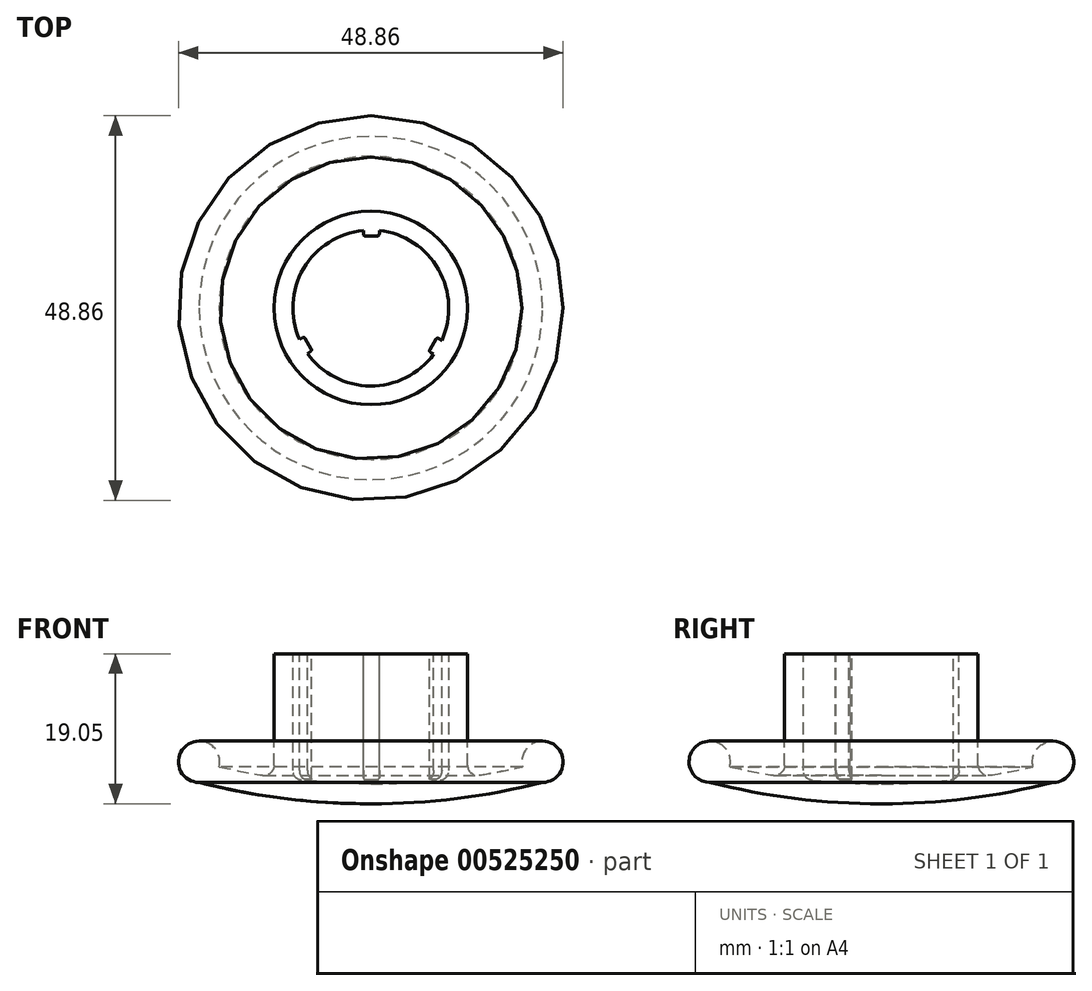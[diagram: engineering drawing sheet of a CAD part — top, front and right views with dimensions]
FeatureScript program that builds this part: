
annotation { "Feature Type Name" : "Feature", "Feature Type Description" : "" }
export const myFeature = defineFeature(function(context is Context, id is Id, definition is map)
    precondition{}
    {
        {
            var Q0;
            Q0=qCreatedBy(makeId("Front.planeOp"),FACE);
            var sketch = newSketch(context, id + "F0", { "sketchPlane" : qUnion([Q0])});
            skLineSegment(sketch, "E0", {"start": v(0, 78.25) * mm, "end": v(0, -60.5) * mm, "construction": true});
            skLineSegment(sketch, "E1", {"start": v(-83.44, 0) * mm, "end": v(73.06, 0) * mm, "construction": true});
            skArc(sketch, "E2", {"start": v(-21.81, 2.72) * mm, "mid": v(-11, 0.68) * mm, "end": v(0, 0) * mm});
            skArc(sketch, "E3", {"start": v(-8.78, 2.99) * mm, "mid": v(-4.4, 2.65) * mm, "end": v(0, 2.54) * mm});
            skLineSegment(sketch, "E4.bottom", {"start": v(-12.29, 19.05) * mm, "end": v(-9.9, 19.05) * mm});
            skLineSegment(sketch, "E4.left", {"start": v(-12.29, 19.05) * mm, "end": v(-12.29, 4.88) * mm});
            skLineSegment(sketch, "E4.right", {"start": v(-9.9, 19.05) * mm, "end": v(-9.9, 4.23) * mm});
            skLineSegment(sketch, "E5", {"start": v(0, 2.54) * mm, "end": v(0, 0) * mm});
            skArc(sketch, "E6.trimOffspring", {"start": v(-19.26, 4.72) * mm, "mid": v(-16.51, 4.13) * mm, "end": v(-13.74, 3.64) * mm});
            skArc(sketch, "E7", {"start": v(-19.26, 4.72) * mm, "mid": v(-23.43, 7.4) * mm, "end": v(-21.81, 2.72) * mm});
            skPoint(sketch, "E8.visualSharp", {"position": v(-12.29, 3.42) * mm});
            skArc(sketch, "E8.filletArc", {"start": v(-13.74, 3.64) * mm, "mid": v(-12.73, 3.92) * mm, "end": v(-12.29, 4.88) * mm});
            skPoint(sketch, "E9.visualSharp", {"position": v(-9.9, 3.11) * mm});
            skArc(sketch, "E9.filletArc", {"start": v(-9.9, 4.23) * mm, "mid": v(-9.58, 3.4) * mm, "end": v(-8.78, 2.99) * mm});
            skSolve(sketch);
        }
        {
            var Q0;
            Q0 = qSketchRegion(id + "F0", true);
            var Q1;
            Q1=sQuery(id+"F0.wireOp",EDGE,"E0");
            revolve(context, id + "F1", {"entities" : qUnion([Q0]), "axis" : qUnion([Q1]), "revolveType" : RevolveType.FULL});
        }
        {
            var Q0;
            Q0=makeQuery(id+"F1.opRevolve","SWEPT_FACE",FACE,{"disambiguationData":[OSD([sQuery(id+"F0.wireOp",EDGE,"E4.bottom")])]});
            var sketch = newSketch(context, id + "F2", { "sketchPlane" : qUnion([Q0])});
            skLineSegment(sketch, "E10.bottom", {"start": v(-0.95, 12.05) * mm, "end": v(0.17, 12.05) * mm});
            skLineSegment(sketch, "E10.top", {"start": v(-0.7, 9.14) * mm, "end": v(0, 9.14) * mm});
            skLineSegment(sketch, "E10.left", {"start": v(-0.95, 12.05) * mm, "end": v(-0.95, 9.4) * mm});
            skLineSegment(sketch, "E11.MirrorCS", {"start": v(0.82, 9.14) * mm, "end": v(0, 9.14) * mm});
            skLineSegment(sketch, "E12.MirrorCS", {"start": v(1.08, 12.04) * mm, "end": v(0.13, 12.04) * mm});
            skLineSegment(sketch, "E13.MirrorCS", {"start": v(1.08, 12.04) * mm, "end": v(1.08, 9.4) * mm});
            skLineSegment(sketch, "E14.1.0", {"start": v(-9.96, -6.85) * mm, "end": v(-7.66, -5.52) * mm});
            skLineSegment(sketch, "E14.1.1", {"start": v(-10.97, -5.09) * mm, "end": v(-8.68, -3.77) * mm});
            skLineSegment(sketch, "E14.1.2", {"start": v(-8.33, -3.86) * mm, "end": v(-7.92, -4.57) * mm});
            skLineSegment(sketch, "E14.1.3", {"start": v(-10.97, -5.09) * mm, "end": v(-10.5, -5.9) * mm});
            skLineSegment(sketch, "E14.1.4", {"start": v(-7.57, -5.18) * mm, "end": v(-7.92, -4.57) * mm});
            skLineSegment(sketch, "E14.1.5", {"start": v(-9.96, -6.85) * mm, "end": v(-10.52, -5.88) * mm});
            skLineSegment(sketch, "E14.2.0", {"start": v(10.91, -5.2) * mm, "end": v(8.62, -3.87) * mm});
            skLineSegment(sketch, "E14.2.1", {"start": v(9.89, -6.95) * mm, "end": v(7.6, -5.63) * mm});
            skLineSegment(sketch, "E14.2.2", {"start": v(7.5, -5.29) * mm, "end": v(7.92, -4.57) * mm});
            skLineSegment(sketch, "E14.2.3", {"start": v(9.89, -6.95) * mm, "end": v(10.36, -6.13) * mm});
            skLineSegment(sketch, "E14.2.4", {"start": v(8.27, -3.97) * mm, "end": v(7.92, -4.57) * mm});
            skLineSegment(sketch, "E14.2.5", {"start": v(10.91, -5.2) * mm, "end": v(10.35, -6.17) * mm});
            skPoint(sketch, "E14.center", {"position": v(0, 0) * mm});
            skCircle(sketch, "E15", {"center": v(0, 0) * mm, "radius": 9.14 * mm, "construction": true});
            skLineSegment(sketch, "E16", {"start": v(0, 16.03) * mm, "end": v(0, -3.78) * mm, "construction": true});
            skPoint(sketch, "E17.visualSharp", {"position": v(-0.95, 9.14) * mm});
            skArc(sketch, "E17.filletArc", {"start": v(-0.95, 9.4) * mm, "mid": v(-0.88, 9.22) * mm, "end": v(-0.7, 9.14) * mm});
            skPoint(sketch, "E18.visualSharp", {"position": v(1.08, 9.14) * mm});
            skArc(sketch, "E18.filletArc", {"start": v(0.82, 9.14) * mm, "mid": v(1, 9.22) * mm, "end": v(1.08, 9.4) * mm});
            skPoint(sketch, "E19.visualSharp", {"position": v(8.4, -3.75) * mm});
            skArc(sketch, "E19.filletArc", {"start": v(8.62, -3.87) * mm, "mid": v(8.42, -3.85) * mm, "end": v(8.27, -3.97) * mm});
            skPoint(sketch, "E20.visualSharp", {"position": v(7.38, -5.5) * mm});
            skArc(sketch, "E20.filletArc", {"start": v(7.5, -5.29) * mm, "mid": v(7.48, -5.48) * mm, "end": v(7.6, -5.63) * mm});
            skPoint(sketch, "E21.visualSharp", {"position": v(-8.46, -3.64) * mm});
            skArc(sketch, "E21.filletArc", {"start": v(-8.33, -3.86) * mm, "mid": v(-8.49, -3.74) * mm, "end": v(-8.68, -3.77) * mm});
            skPoint(sketch, "E22.visualSharp", {"position": v(-7.44, -5.4) * mm});
            skArc(sketch, "E22.filletArc", {"start": v(-7.66, -5.52) * mm, "mid": v(-7.54, -5.37) * mm, "end": v(-7.57, -5.18) * mm});
            skSolve(sketch);
        }
        {
            var Q0;
            Q0=makeQuery(id+"F2.imprint","IMPRINT",FACE,{"disambiguationData":[TD([[makeQuery(id+"F2.imprint","IMPRINT",EDGE,{"derivedFrom":sQuery(id+"F2.wireOp",EDGE,"E14.1.2")}),-1.0]])]});
            var Q1;
            Q1=makeQuery(id+"F2.imprint","IMPRINT",FACE,{"disambiguationData":[TD([[makeQuery(id+"F2.imprint","IMPRINT",EDGE,{"derivedFrom":sQuery(id+"F2.wireOp",EDGE,"E14.2.2")}),-1.0]])]});
            var Q2;
            Q2=makeQuery(id+"F2.imprint","IMPRINT",FACE,{"disambiguationData":[TD([[makeQuery(id+"F2.imprint","IMPRINT",EDGE,{"derivedFrom":sQuery(id+"F2.wireOp",EDGE,"E10.top")}),1.0]])]});
            extrude(context, id + "F3", {"entities" : qUnion([Q0, Q1, Q2]), "operationType" : NewBodyOperationType.ADD, "endBound" : BoundingType.UP_TO_NEXT, "oppositeDirection" : true, "depth" : 25.4 * mm, "offsetDistance" : 25.4 * mm});
        }
    });
